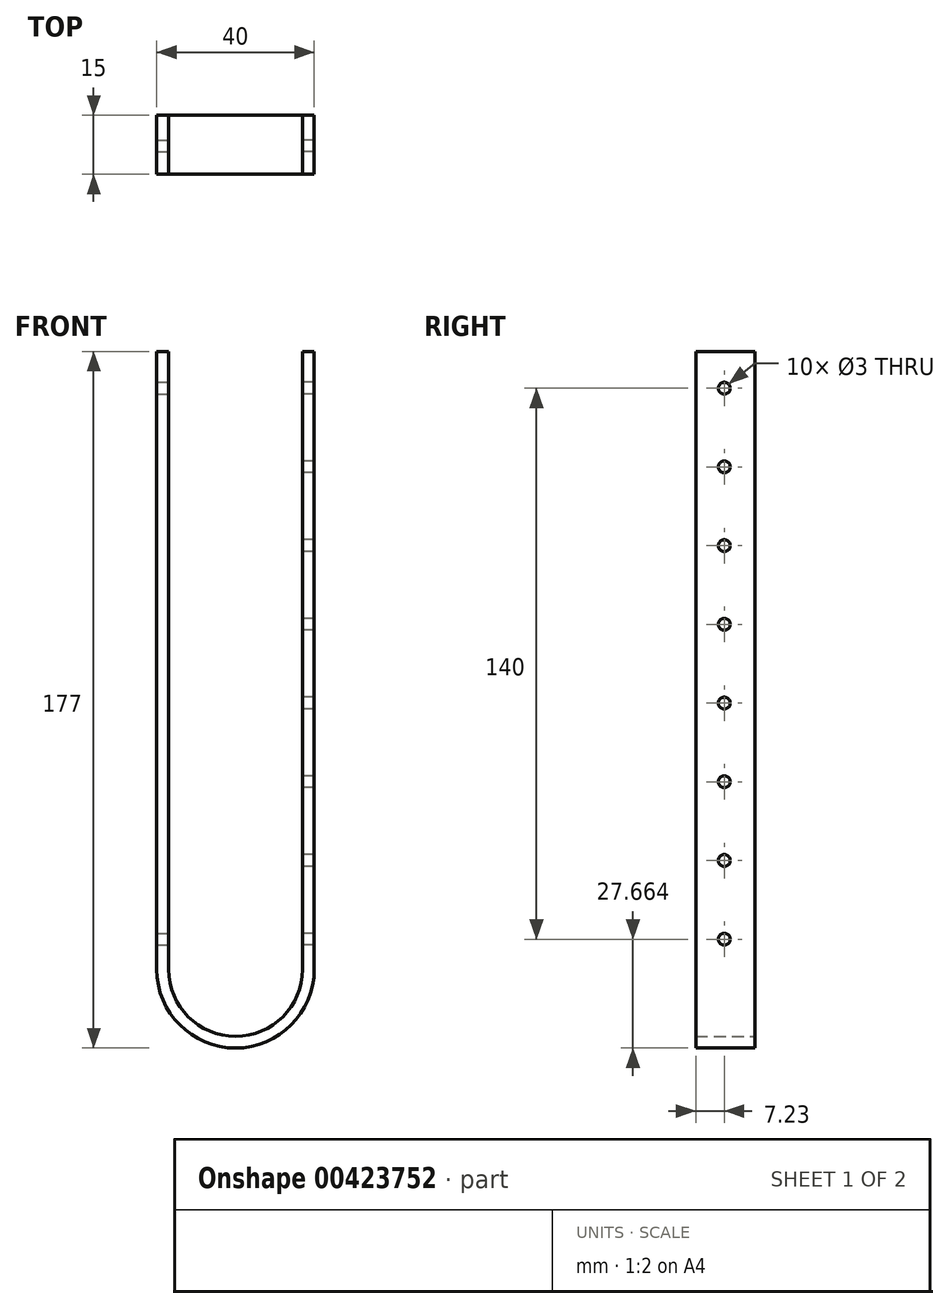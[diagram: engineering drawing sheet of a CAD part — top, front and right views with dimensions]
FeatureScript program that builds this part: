
annotation { "Feature Type Name" : "Feature", "Feature Type Description" : "" }
export const myFeature = defineFeature(function(context is Context, id is Id, definition is map)
    precondition{}
    {
        {
            var Q0;
            Q0=qCreatedBy(makeId("Front.planeOp"),FACE);
            var sketch = newSketch(context, id + "F0", { "sketchPlane" : qUnion([Q0])});
            skLineSegment(sketch, "E0.left", {"start": v(-21.17, 28.59) * mm, "end": v(-21.17, -128.41) * mm});
            skLineSegment(sketch, "E0.right", {"start": v(18.83, 28.59) * mm, "end": v(18.83, -128.41) * mm});
            skArc(sketch, "E1", {"start": v(-21.17, -128.41) * mm, "mid": v(-1.17, -148.41) * mm, "end": v(18.83, -128.41) * mm});
            skLineSegment(sketch, "E2", {"start": v(-21.17, 28.59) * mm, "end": v(-18.17, 28.59) * mm});
            skLineSegment(sketch, "E3.0", {"start": v(-18.17, 28.59) * mm, "end": v(-18.17, -128.41) * mm});
            skArc(sketch, "E4.0", {"start": v(-18.17, -128.41) * mm, "mid": v(-1.17, -145.41) * mm, "end": v(15.83, -128.41) * mm});
            skLineSegment(sketch, "E5.0", {"start": v(15.83, 28.59) * mm, "end": v(15.83, -128.41) * mm});
            skLineSegment(sketch, "E6.trimOffspring", {"start": v(15.83, 28.59) * mm, "end": v(18.83, 28.59) * mm});
            skSolve(sketch);
        }
        {
            var Q0;
            Q0=qSketchRegion(id+"F0",true);
            var Q1;
            Q1=qSketchRegion(id+"F2",true);
            extrude(context, id + "F1", {"entities" : qUnion([Q0, Q1]), "depth" : 15 * mm});
        }
        {
            var Q0;
            Q0=qCreatedBy(makeId("Right.planeOp"),FACE);
            var sketch = newSketch(context, id + "F2", { "sketchPlane" : qUnion([Q0])});
            skCircle(sketch, "E7", {"center": v(-7.77, 19.25) * mm, "radius": 1.5 * mm});
            skCircle(sketch, "E8", {"center": v(-7.77, -0.75) * mm, "radius": 1.5 * mm});
            skCircle(sketch, "E9", {"center": v(-7.77, -20.75) * mm, "radius": 1.5 * mm});
            skCircle(sketch, "E10", {"center": v(-7.77, -40.75) * mm, "radius": 1.5 * mm});
            skCircle(sketch, "E11", {"center": v(-7.77, -60.75) * mm, "radius": 1.5 * mm});
            skCircle(sketch, "E12", {"center": v(-7.77, -80.75) * mm, "radius": 1.5 * mm});
            skCircle(sketch, "E13", {"center": v(-7.77, -100.75) * mm, "radius": 1.5 * mm});
            skCircle(sketch, "E14", {"center": v(-7.77, -120.75) * mm, "radius": 1.5 * mm});
            skLineSegment(sketch, "E15", {"start": v(-7.77, -120.75) * mm, "end": v(-7.77, -100.75) * mm});
            skLineSegment(sketch, "E16", {"start": v(-7.77, -100.75) * mm, "end": v(-7.77, -80.75) * mm});
            skLineSegment(sketch, "E17", {"start": v(-7.77, -60.75) * mm, "end": v(-7.77, -80.75) * mm});
            skLineSegment(sketch, "E18", {"start": v(-7.77, -20.75) * mm, "end": v(-7.77, -40.75) * mm});
            skLineSegment(sketch, "E19", {"start": v(-7.77, -40.75) * mm, "end": v(-7.77, -60.75) * mm});
            skLineSegment(sketch, "E20", {"start": v(-7.77, 19.25) * mm, "end": v(-7.77, 29.25) * mm});
            skSolve(sketch);
        }
        {
            var Q0;
            Q0=sQuery(id+"F2.wireOp",VERTEX,"E8.center");
            var Q1;
            Q1=sQuery(id+"F2.wireOp",VERTEX,"E9.center");
            var Q2;
            Q2=sQuery(id+"F2.wireOp",VERTEX,"E10.center");
            var Q3;
            Q3=sQuery(id+"F2.wireOp",VERTEX,"E11.center");
            var Q4;
            Q4=sQuery(id+"F2.wireOp",VERTEX,"E12.center");
            var Q5;
            Q5=sQuery(id+"F2.wireOp",VERTEX,"E13.center");
            var Q6;
            Q6=sQuery(id+"F2.wireOp",VERTEX,"E14.center");
            var Q7;
            Q7=sQuery(id+"F2.wireOp",VERTEX,"E7.center");
            var Q8;
            Q8=makeQuery(id+"F1.opExtrude","SWEPT_BODY",BODY,{"disambiguationData":[OSD([sQuery(id+"F0.wireOp",EDGE,"E0.left"),sQuery(id+"F0.wireOp",EDGE,"E0.right"),sQuery(id+"F0.wireOp",EDGE,"E1"),sQuery(id+"F0.wireOp",EDGE,"E2"),sQuery(id+"F0.wireOp",EDGE,"E3.0"),sQuery(id+"F0.wireOp",EDGE,"E4.0"),sQuery(id+"F0.wireOp",EDGE,"E5.0"),sQuery(id+"F0.wireOp",EDGE,"E6.trimOffspring")])]});
            hole(context, id + "F3", {"style" : HoleStyle.SIMPLE, "endStyle" : HoleEndStyle.THROUGH, "oppositeDirection" : true, "holeDiameter" : 3 * mm, "isTappedThrough" : true, "tappedDepth" : 12 * mm, "tapClearance" : 3, "locations" : qUnion([Q0, Q1, Q2, Q3, Q4, Q5, Q6, Q7]), "scope" : qUnion([Q8])});
        }
        {
            var Q0;
            Q0=sQuery(id+"F2.wireOp",VERTEX,"E7.center");
            var Q1;
            Q1=sQuery(id+"F2.wireOp",VERTEX,"E14.center");
            var Q2;
            Q2=makeQuery(id+"F1.opExtrude","SWEPT_BODY",BODY,{"disambiguationData":[OSD([sQuery(id+"F0.wireOp",EDGE,"E0.left"),sQuery(id+"F0.wireOp",EDGE,"E0.right"),sQuery(id+"F0.wireOp",EDGE,"E1"),sQuery(id+"F0.wireOp",EDGE,"E2"),sQuery(id+"F0.wireOp",EDGE,"E3.0"),sQuery(id+"F0.wireOp",EDGE,"E4.0"),sQuery(id+"F0.wireOp",EDGE,"E5.0"),sQuery(id+"F0.wireOp",EDGE,"E6.trimOffspring")])]});
            hole(context, id + "F4", {"style" : HoleStyle.SIMPLE, "endStyle" : HoleEndStyle.THROUGH, "holeDiameter" : 3 * mm, "isTappedThrough" : true, "tappedDepth" : 12 * mm, "tapClearance" : 3, "locations" : qUnion([Q0, Q1]), "scope" : qUnion([Q2])});
        }
    });
